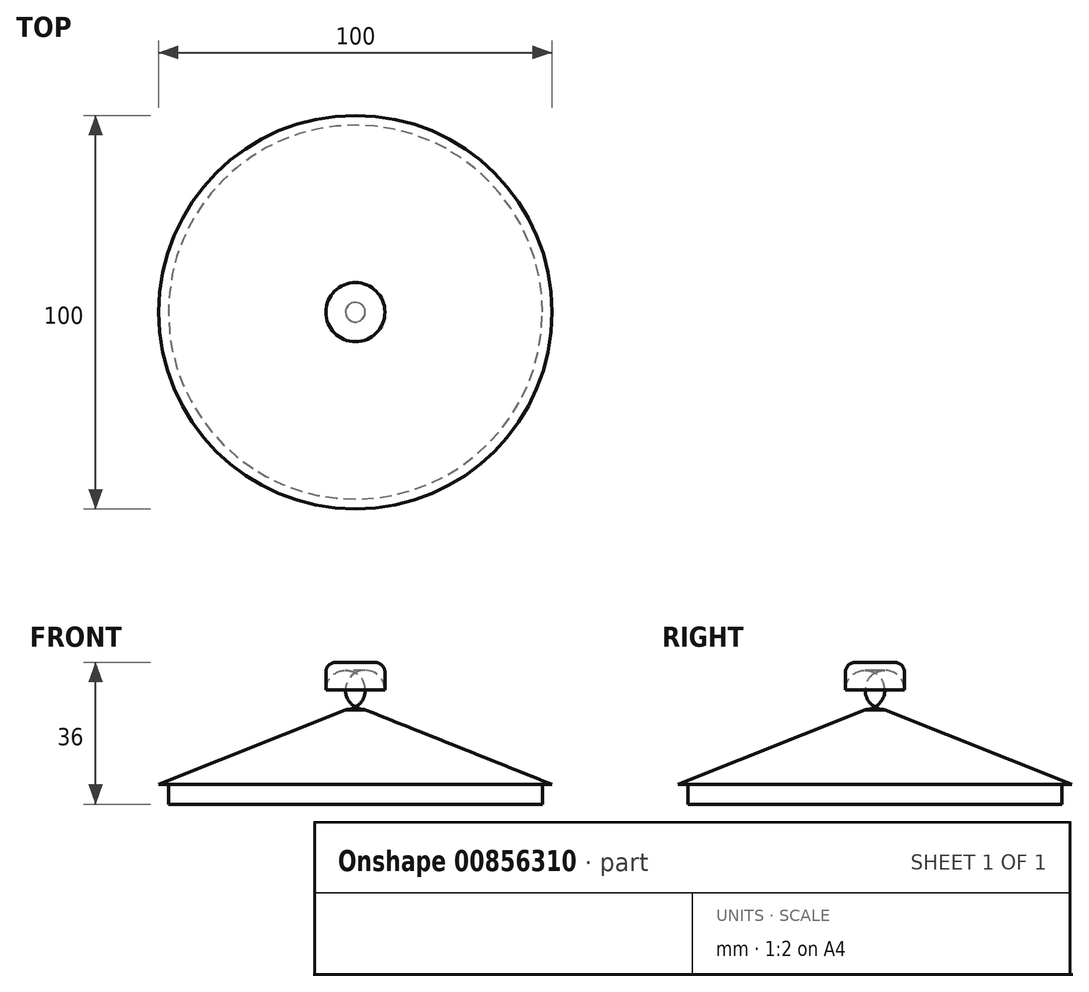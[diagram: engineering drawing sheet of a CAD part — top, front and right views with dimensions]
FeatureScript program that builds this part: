
annotation { "Feature Type Name" : "Feature", "Feature Type Description" : "" }
export const myFeature = defineFeature(function(context is Context, id is Id, definition is map)
    precondition{}
    {
        {
            var Q0;
            Q0=qCreatedBy(makeId("Top.planeOp"),FACE);
            var sketch = newSketch(context, id + "F0", { "sketchPlane" : qUnion([Q0])});
            skCircle(sketch, "E0", {"center": v(0, 0) * mm, "radius": 50 * mm});
            skSolve(sketch);
        }
        {
            var Q0;
            Q0=qCreatedBy(makeId("Top.planeOp"),FACE);
            cPlane(context, id + "F1", {"entities" : qUnion([Q0]), "cplaneType" : CPlaneType.OFFSET, "offset" : 19 * mm, "width" : 150 * mm, "height" : 150 * mm});
        }
        {
            var Q0;
            Q0=qCreatedBy(id+"F1.planeOp",FACE);
            var sketch = newSketch(context, id + "F2", { "sketchPlane" : qUnion([Q0])});
            skCircle(sketch, "E1", {"center": v(0, 0) * mm, "radius": 2.5 * mm});
            skSolve(sketch);
        }
        {
            var Q0;
            Q0 = qSketchRegion(id + "F2", true);
            var Q1;
            Q1 = qSketchRegion(id + "F0", true);
            loft(context, id + "F3", {"sheetProfilesArray" : [{ "sheetProfileEntities" : qUnion([Q0]) }, { "sheetProfileEntities" : qUnion([Q1]) }]});
        }
        {
            var Q0;
            Q0=makeQuery(id+"F2.imprint","IMPRINT",FACE,{"disambiguationData":[TD([[makeQuery(id+"F2.imprint","IMPRINT",EDGE,{"derivedFrom":sQuery(id+"F2.wireOp",EDGE,"E1")}),1.0]])]});
            var Q1;
            Q1=makeQuery(id+"F0.imprint","IMPRINT",FACE,{"disambiguationData":[TD([[makeQuery(id+"F0.imprint","IMPRINT",EDGE,{"derivedFrom":sQuery(id+"F0.wireOp",EDGE,"E0")}),1.0]])]});
            loft(context, id + "F4", {"sheetProfilesArray" : [{ "sheetProfileEntities" : qUnion([Q0]) }, { "sheetProfileEntities" : qUnion([Q1]) }]});
        }
        {
            var Q0;
            Q0=qCreatedBy(id+"F1.planeOp",FACE);
            var sketch = newSketch(context, id + "F5", { "sketchPlane" : qUnion([Q0])});
            skCircle(sketch, "E2", {"center": v(0, 0) * mm, "radius": 7.5 * mm});
            skSolve(sketch);
        }
        {
            var Q0;
            Q0=makeQuery(id+"F5.imprint","IMPRINT",FACE,{"disambiguationData":[TD([[makeQuery(id+"F5.imprint","IMPRINT",EDGE,{"derivedFrom":sQuery(id+"F5.wireOp",EDGE,"E2")}),1.0]])]});
            extrude(context, id + "F6", {"entities" : qUnion([Q0]), "operationType" : NewBodyOperationType.ADD, "depth" : 12 * mm, "offsetDistance" : 25 * mm});
        }
        {
            var Q0;
            Q0=makeQuery(id+"F6.opExtrude","CAP_EDGE",EDGE,{"disambiguationData":[OSD([sQuery(id+"F5.wireOp",EDGE,"E2")])],"isStart":false});
            fillet(context, id + "F7", {"entities" : qUnion([Q0]), "radius" : 2.5 * mm, "tangentPropagation" : true, "allowEdgeOverflow" : false});
        }
        {
            var Q0;
            Q0=makeQuery(id+"F6.opExtrude","CAP_EDGE",EDGE,{"disambiguationData":[OSD([sQuery(id+"F5.wireOp",EDGE,"E2")])],"isStart":true});
            fillet(context, id + "F8", {"entities" : qUnion([Q0]), "radius" : 5 * mm, "tangentPropagation" : true, "allowEdgeOverflow" : false});
        }
        {
            var Q0;
            Q0=qCreatedBy(makeId("Top.planeOp"),FACE);
            var sketch = newSketch(context, id + "F9", { "sketchPlane" : qUnion([Q0])});
            skCircle(sketch, "E3", {"center": v(0, 0) * mm, "radius": 47.5 * mm});
            skSolve(sketch);
        }
        {
            var Q0;
            Q0=makeQuery(id+"F9.imprint","IMPRINT",FACE,{"disambiguationData":[TD([[makeQuery(id+"F9.imprint","IMPRINT",EDGE,{"derivedFrom":sQuery(id+"F9.wireOp",EDGE,"E3")}),1.0]])]});
            extrude(context, id + "F10", {"entities" : qUnion([Q0]), "operationType" : NewBodyOperationType.ADD, "oppositeDirection" : true, "depth" : 5 * mm, "offsetDistance" : 25 * mm});
        }
    });
